# Revit family: Faucet-Kitchen-Grohe-Grohe_Blue_Professional-31608_Series
name_source: partatom
category: Plumbing Fixtures
units: mm (PartAtom-declared; Revit-internal decimal feet)

## family parameters
Always vertical = No
Cut with Voids When Loaded = No
OmniClass Number = 23.45.55.14
OmniClass Title = Single Faucets
Part Type = Normal
Room Calculation Point = No
Round Connector Dimension = Use Diameter
Shared = Yes
Work Plane-Based = Yes

## types (2) — shared parameters
ADA Compliant = Yes
Assembly Code = D2020300
CW Connection = No
CWFU = 1.5
CalGreen Compliant = Yes
Default Elevation = 0"
Description = Grohe Blue Professional Kitchen Faucet Starter Kit
Flow Rate = 1.75 gpm (6.6 L/min)
HW Connection = No
HWFU = 1.5
Height = 14 1/2"
IAPMO Compliance = NSF 61, US Federal and State material regulations,ICC/ANSI A117.1,Energy Policy Act of 1992,ASME A112.18.1/CSA B125.1
Installation Type = Deck-Mounted
Length = 8 3/4"
Manufacturer = Grohe
Price = Prices may vary. Please consult Manufacturer Representative for most up-to-date price list.
Product Documentation Link = https://americanstandard.box.com
Product Page URL = https://www.grohe.ca
Shipping Weight = 62.49 lb
Tempered Water Connection = Yes
Tempered Water Connection Diameter = 3/8"
URL = https://www.grohe.us
Update Date = 03/07/2022
Vent Connection = No
Warranty Documentation Link = https://cdn.cloud.grohe.com
Waste Connection = No
Width = 6 5/32"
zero-valued in all types: WFU

## per-type parameters (varying)
| type | Finish | Material |
| 31608002 | Brass-Grohe-002- StarLight Chrome | Brass-Grohe-002- StarLight Chrome |
| 31608DC2 | Brass-Grohe-DC2- SuperSteel | Brass-Grohe-DC2- SuperSteel |

note: column(s) folded — value = type name in every type: Model

## geometry (parser evidence)
native form markers: Sweep x2
no freeform markers — native parametric forms only
